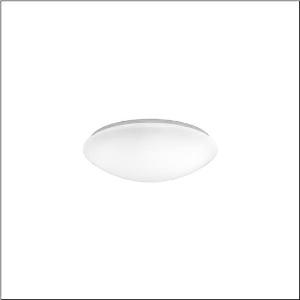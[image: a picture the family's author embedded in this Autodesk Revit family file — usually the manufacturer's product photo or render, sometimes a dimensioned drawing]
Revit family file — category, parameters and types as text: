
# Revit family: round_31_b_5pja010001a
name_source: partatom
category: Lighting Fixtures
units: mm (PartAtom-declared; Revit-internal decimal feet)

## family parameters
Cut with Voids When Loaded = No
Host = Face
Light Source = No
Part Type = Normal
Room Calculation Point = No
Round Connector Dimension = Use Diameter
Shared = No

## types (1)
- Round 31 B (1 x LED, 1800 lm, 15 W, 3000K)
    Apparent Load = 15 VA
    CIE Flux Codes = 42 71 89 88 100
    Color Rendering = 80
    Color Temperature = 3000K
    Default Elevation = 1800 mm  [stored 5.90551 ft]
    Description = Round 31 B, wall and ceiling luminaire, primary optical cover: enclosure, of PMMA, light emission: direct distribution, primary light characteristic: symmetric, installation type: surface-mounted, LED, rated luminous flux: 1.800lm, luminous efficacy: 120lm/W, light colour: 830, colour temperature: 3000K, with terminal, 3-pole, max. 2.5mm², mains connection: 230V, AC, 50/60Hz, rated input power: 15W, luminaire housing, round, of steel, white, diameter: 290mm, height: 85mm, protection rating (complete): IP40, insulation class (complete): insulation class I (protective earthing), certification: CE, impact resistance: IK02, permissible operating ambient temperature: -20..+25°C, packaging unit: 1 piece
    Height = 85 mm
    Lamp = 1 x LED
    Lamp Light Flux = 1800 lm
    Lamp Power = 15 W
    Lamp count = 1
    Length = 290 mm
    Luminous efficacy = 120 lm/W
    Manufacturer = Siteco
    ModVariant = No
    Model = 5PJA010001A
    Mounting Place = Ceiling
    Mounting Type = Surface mounted
    Number of Poles = 1
    OnlyDefault = Yes
    Power Factor = 1
    Product Name = Round 31 B
    Product group = wall and ceiling luminaire
    ProductGroupID = 302
    Protection Class = Protection class I
    Protection Degree = IP 40
    RLX_Detail_Level = 1
    RLX_Emergency_Light_Flux = 0 lm
    RLX_Emergency_Type = 0
    RLX_Emergency_Type_DB = No
    RlxData = <blob elided: 9237 chars, md5=c56bd151>
    Socket = socket
    Standby Power = 0 W
    System Light Flux = 1800 lm
    System Power = 15 W
    Type Comments = Product without accessories
    Type Image = l_1258346.jpg
    URL = http://relux.com
    VarID = ---
    Voltage = 0 V
    Weight = 0.00 kg
    Width = 0 mm  [stored 0 ft]

note: [stored X ft] marks values corroborated as IEEE doubles in the binary element streams (Revit-internal decimal feet)

## geometry (parser evidence)
native form markers: Sweep x10
no freeform markers — native parametric forms only
